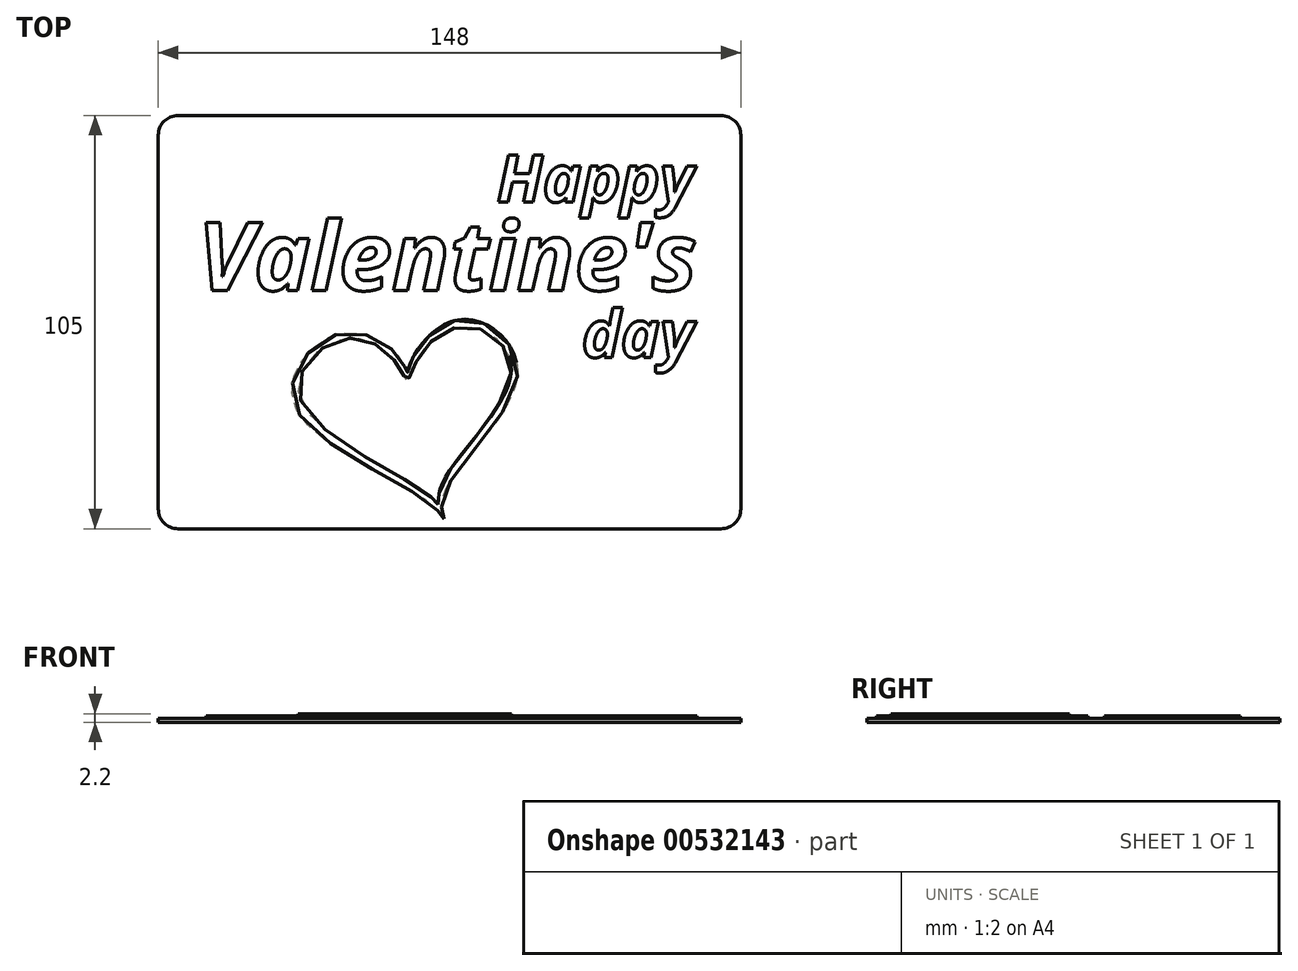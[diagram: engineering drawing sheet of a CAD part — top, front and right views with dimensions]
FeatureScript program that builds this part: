
annotation { "Feature Type Name" : "Feature", "Feature Type Description" : "" }
export const myFeature = defineFeature(function(context is Context, id is Id, definition is map)
    precondition{}
    {
        {
            var Q0;
            Q0=qCreatedBy(makeId("Top.planeOp"),FACE);
            var sketch = newSketch(context, id + "F0", { "sketchPlane" : qUnion([Q0])});
            skLineSegment(sketch, "E0.bottom", {"start": v(69, 52.5) * mm, "end": v(-69, 52.5) * mm});
            skLineSegment(sketch, "E0.top", {"start": v(69, -52.5) * mm, "end": v(-69, -52.5) * mm});
            skLineSegment(sketch, "E0.left", {"start": v(74, 47.5) * mm, "end": v(74, -47.5) * mm});
            skLineSegment(sketch, "E0.right", {"start": v(-74, 47.5) * mm, "end": v(-74, -47.5) * mm});
            skPoint(sketch, "E0.middle", {"position": v(0, 0) * mm});
            skPoint(sketch, "E1.visualSharp", {"position": v(-74, 52.5) * mm});
            skArc(sketch, "E1.filletArc", {"start": v(-69, 52.5) * mm, "mid": v(-72.54, 51.04) * mm, "end": v(-74, 47.5) * mm});
            skPoint(sketch, "E2.visualSharp", {"position": v(74, 52.5) * mm});
            skArc(sketch, "E2.filletArc", {"start": v(74, 47.5) * mm, "mid": v(72.54, 51.04) * mm, "end": v(69, 52.5) * mm});
            skPoint(sketch, "E3.visualSharp", {"position": v(74, -52.5) * mm});
            skArc(sketch, "E3.filletArc", {"start": v(69, -52.5) * mm, "mid": v(72.54, -51.04) * mm, "end": v(74, -47.5) * mm});
            skPoint(sketch, "E4.visualSharp", {"position": v(-74, -52.5) * mm});
            skArc(sketch, "E4.filletArc", {"start": v(-74, -47.5) * mm, "mid": v(-72.54, -51.04) * mm, "end": v(-69, -52.5) * mm});
            skSolve(sketch);
        }
        {
            var Q0;
            Q0 = qSketchRegion(id + "F0", true);
            extrude(context, id + "F1", {"entities" : qUnion([Q0]), "depth" : 1 * mm, "offsetDistance" : 25 * mm});
        }
        {
            var Q0;
            Q0=makeQuery(id+"F1.opExtrude","CAP_FACE",FACE,{"disambiguationData":[OSD([sQuery(id+"F0.wireOp",EDGE,"E0.bottom"),sQuery(id+"F0.wireOp",EDGE,"E0.top"),sQuery(id+"F0.wireOp",EDGE,"E0.left"),sQuery(id+"F0.wireOp",EDGE,"E0.right"),sQuery(id+"F0.wireOp",EDGE,"E1.filletArc"),sQuery(id+"F0.wireOp",EDGE,"E2.filletArc"),sQuery(id+"F0.wireOp",EDGE,"E3.filletArc"),sQuery(id+"F0.wireOp",EDGE,"E4.filletArc")])],"isStart":false});
            var sketch = newSketch(context, id + "F2", { "sketchPlane" : qUnion([Q0])});
            skText(sketch, "E5", { "text": "Happy", "fontName": "NotoSans-BoldItalic.ttf"});
            skText(sketch, "E6", { "text": "Valentine\'s", "fontName": "NotoSans-BoldItalic.ttf"});
            skText(sketch, "E7", { "text": "day", "fontName": "NotoSans-BoldItalic.ttf"});
            skLineSegment(sketch, "E8.bottom", {"start": v(74, 52.5) * mm, "end": v(-74, 52.5) * mm, "construction": true});
            skLineSegment(sketch, "E8.top", {"start": v(74, -52.5) * mm, "end": v(-74, -52.5) * mm, "construction": true});
            skLineSegment(sketch, "E8.left", {"start": v(74, 52.5) * mm, "end": v(74, -52.5) * mm, "construction": true});
            skLineSegment(sketch, "E8.right", {"start": v(-74, 52.5) * mm, "end": v(-74, -52.5) * mm, "construction": true});
            skPoint(sketch, "E8.middle", {"position": v(0, 0) * mm});
            skFitSpline(sketch, "E9", {"points": [v(-1.34, -50.07) * mm, v(-5.58, -45.58) * mm, v(-39.61, -20.52) * mm, v(-27.67, -2.9) * mm, v(-12.32, -9.64) * mm, v(-10.82, -12.88) * mm, v(-9.7, -9.76) * mm, v(3.4, 0.72) * mm, v(17.25, -13.26) * mm, v(-1.71, -44.33) * mm, v(-1.34, -50.07) * mm]});
            const initialGuessF2  = {"E5": [0.012, 0.0305, 1, 0, 0.012], "E6": [-0.064, 0.00806, 1, 0, 0.01744], "E7": [0.0336, -0.00894, 1, 0, 0.012]};
            skSetInitialGuess(sketch, initialGuessF2);
            skSolve(sketch);
        }
        {
            var Q0;
            Q0 = qSketchRegion(id + "F2", true);
            extrude(context, id + "F3", {"entities" : qUnion([Q0]), "operationType" : NewBodyOperationType.ADD, "depth" : 0.6 * mm, "offsetDistance" : 25 * mm});
        }
        {
            var Q0;
            Q0=makeQuery(id+"F3.opExtrude","CAP_FACE",FACE,{"disambiguationData":[OSD([sQuery(id+"F2.wireOp",EDGE,"E9")])],"isStart":false});
            var sketch = newSketch(context, id + "F4", { "sketchPlane" : qUnion([Q0])});
            skFitSpline(sketch, "E10", {"points": [v(-2.98, -46.33) * mm, v(-5.08, -44) * mm, v(-38.05, -19.23) * mm, v(-26.65, -4.18) * mm, v(-13.6, -10.27) * mm, v(-10.73, -14.7) * mm, v(-8.73, -10.38) * mm, v(3.69, -1.03) * mm, v(15.69, -12.28) * mm, v(-1.7, -40.66) * mm, v(-2.98, -46.33) * mm]});
            skSolve(sketch);
        }
        {
            var Q0;
            Q0=makeQuery(id+"F4.imprint","IMPRINT",FACE,{"disambiguationData":[TD([[makeQuery(id+"F4.imprint","IMPRINT",EDGE,{"derivedFrom":sQuery(id+"F4.wireOp",EDGE,"E10")}),-1.0]])]});
            extrude(context, id + "F5", {"entities" : qUnion([Q0]), "operationType" : NewBodyOperationType.ADD, "depth" : 0.6 * mm, "offsetDistance" : 25 * mm});
        }
    });
